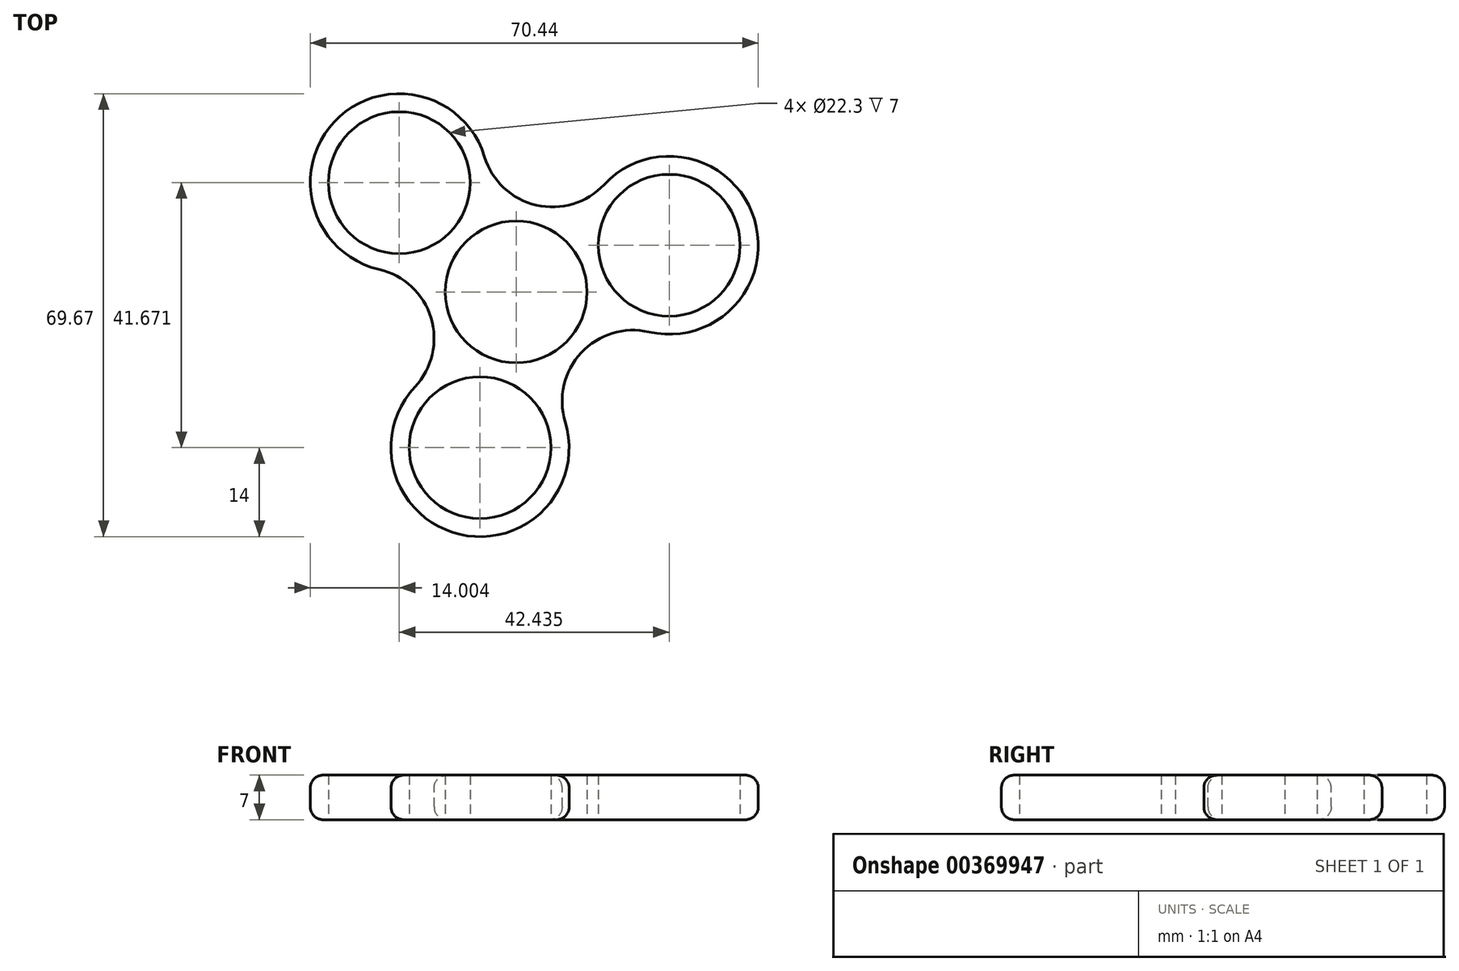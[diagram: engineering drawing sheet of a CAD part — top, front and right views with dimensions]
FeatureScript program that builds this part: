
annotation { "Feature Type Name" : "Feature", "Feature Type Description" : "" }
export const myFeature = defineFeature(function(context is Context, id is Id, definition is map)
    precondition{}
    {
        {
            var Q0;
            Q0=qCreatedBy(makeId("Top.planeOp"),FACE);
            var sketch = newSketch(context, id + "F0", { "sketchPlane" : qUnion([Q0])});
            skCircle(sketch, "E0", {"center": v(0, 0) * mm, "radius": 11.15 * mm});
            skLineSegment(sketch, "E1", {"start": v(0, 0) * mm, "end": v(-18.38, 17.17) * mm});
            skLineSegment(sketch, "E2", {"start": v(0, 0) * mm, "end": v(24.06, 7.33) * mm});
            skLineSegment(sketch, "E3", {"start": v(0, 0) * mm, "end": v(-5.68, -24.5) * mm});
            skCircle(sketch, "E4", {"center": v(-18.38, 17.17) * mm, "radius": 11.15 * mm});
            skCircle(sketch, "E5", {"center": v(24.06, 7.33) * mm, "radius": 11.15 * mm});
            skCircle(sketch, "E6", {"center": v(-5.68, -24.5) * mm, "radius": 11.15 * mm});
            skCircle(sketch, "E7", {"center": v(0, 0) * mm, "radius": 14 * mm});
            skCircle(sketch, "E8", {"center": v(-18.38, 17.17) * mm, "radius": 14 * mm});
            skCircle(sketch, "E9", {"center": v(24.06, 7.33) * mm, "radius": 14 * mm});
            skCircle(sketch, "E10", {"center": v(-5.68, -24.5) * mm, "radius": 14 * mm});
            skLineSegment(sketch, "E11", {"start": v(-18.38, 17.17) * mm, "end": v(-8.82, 27.4) * mm});
            skLineSegment(sketch, "E12", {"start": v(24.06, 7.33) * mm, "end": v(19.98, 20.72) * mm});
            skLineSegment(sketch, "E13", {"start": v(-5.68, -24.5) * mm, "end": v(7.96, -27.66) * mm});
            skLineSegment(sketch, "E14", {"start": v(-5.68, -24.5) * mm, "end": v(-19.32, -21.34) * mm});
            skLineSegment(sketch, "E15", {"start": v(-18.38, 17.17) * mm, "end": v(-27.93, 6.94) * mm});
            skLineSegment(sketch, "E16", {"start": v(24.06, 7.33) * mm, "end": v(28.14, -6.06) * mm});
            skArc(sketch, "E17", {"start": v(-8.82, 27.4) * mm, "mid": v(3.16, 13.64) * mm, "end": v(19.98, 20.72) * mm});
            skArc(sketch, "E18", {"start": v(-19.32, -21.34) * mm, "mid": v(-13.4, -4.08) * mm, "end": v(-27.93, 6.94) * mm});
            skArc(sketch, "E19", {"start": v(28.14, -6.06) * mm, "mid": v(10.23, -9.56) * mm, "end": v(7.96, -27.66) * mm});
            skSolve(sketch);
        }
        {
            var Q0;
            {var subQ0=sQuery(id+"F0.wireOp",EDGE,"E15");var subQ1=sQuery(id+"F0.wireOp",EDGE,"E4");var subQ2=makeQuery(id+"F0.imprint","INTERSECT",VERTEX,{"derivedFrom":[subQ1,subQ0]});Q0=makeQuery(id+"F0.imprint","IMPRINT",FACE,{"disambiguationData":[TD([[makeQuery(id+"F0.imprint","IMPRINT",EDGE,{"disambiguationData":[TD([[subQ2,1.0]])],"derivedFrom":subQ1}),-1.0]])]});}
            var Q1;
            {var subQ0=sQuery(id+"F0.wireOp",EDGE,"E17");var subQ2=sQuery(id+"F0.wireOp",EDGE,"E8");var subQ6=makeQuery(id+"F0.imprint","INTERSECT",VERTEX,{"derivedFrom":[subQ2,subQ0]});Q1=makeQuery(id+"F0.imprint","IMPRINT",FACE,{"disambiguationData":[TD([[makeQuery(id+"F0.imprint","IMPRINT",EDGE,{"disambiguationData":[TD([[subQ6,1.0]])],"derivedFrom":subQ2}),1.0]])]});}
            var Q2;
            {var subQ0=sQuery(id+"F0.wireOp",EDGE,"E8");var subQ3=sQuery(id+"F0.wireOp",EDGE,"E7");var subQ5=makeQuery(id+"F0.imprint","INTERSECT",VERTEX,{"disambiguationData":[OD(0.0)],"derivedFrom":[subQ3,subQ0]});Q2=makeQuery(id+"F0.imprint","IMPRINT",FACE,{"disambiguationData":[TD([[makeQuery(id+"F0.imprint","IMPRINT",EDGE,{"disambiguationData":[TD([[subQ5,-1.0]])],"derivedFrom":subQ3}),1.0]])]});}
            var Q3;
            {var subQ0=sQuery(id+"F0.wireOp",EDGE,"E8");var subQ3=sQuery(id+"F0.wireOp",EDGE,"E7");var subQ5=makeQuery(id+"F0.imprint","INTERSECT",VERTEX,{"disambiguationData":[OD(1.0)],"derivedFrom":[subQ3,subQ0]});Q3=makeQuery(id+"F0.imprint","IMPRINT",FACE,{"disambiguationData":[TD([[makeQuery(id+"F0.imprint","IMPRINT",EDGE,{"disambiguationData":[TD([[subQ5,1.0]])],"derivedFrom":subQ3}),1.0]])]});}
            var Q4;
            {var subQ0=sQuery(id+"F0.wireOp",EDGE,"E18");var subQ1=sQuery(id+"F0.wireOp",EDGE,"E8");var subQ2=makeQuery(id+"F0.imprint","INTERSECT",VERTEX,{"derivedFrom":[subQ1,subQ0]});Q4=makeQuery(id+"F0.imprint","IMPRINT",FACE,{"disambiguationData":[TD([[makeQuery(id+"F0.imprint","IMPRINT",EDGE,{"disambiguationData":[TD([[subQ2,-1.0]])],"derivedFrom":subQ1}),1.0]])]});}
            var Q5;
            {var subQ0=sQuery(id+"F0.wireOp",EDGE,"E18");var subQ2=sQuery(id+"F0.wireOp",EDGE,"E10");var subQ6=makeQuery(id+"F0.imprint","INTERSECT",VERTEX,{"derivedFrom":[subQ2,subQ0]});Q5=makeQuery(id+"F0.imprint","IMPRINT",FACE,{"disambiguationData":[TD([[makeQuery(id+"F0.imprint","IMPRINT",EDGE,{"disambiguationData":[TD([[subQ6,1.0]])],"derivedFrom":subQ2}),1.0]])]});}
            var Q6;
            {var subQ0=sQuery(id+"F0.wireOp",EDGE,"E10");var subQ3=sQuery(id+"F0.wireOp",EDGE,"E7");var subQ5=makeQuery(id+"F0.imprint","INTERSECT",VERTEX,{"disambiguationData":[OD(0.0)],"derivedFrom":[subQ3,subQ0]});Q6=makeQuery(id+"F0.imprint","IMPRINT",FACE,{"disambiguationData":[TD([[makeQuery(id+"F0.imprint","IMPRINT",EDGE,{"disambiguationData":[TD([[subQ5,-1.0]])],"derivedFrom":subQ3}),1.0]])]});}
            var Q7;
            {var subQ0=sQuery(id+"F0.wireOp",EDGE,"E10");var subQ3=sQuery(id+"F0.wireOp",EDGE,"E7");var subQ5=makeQuery(id+"F0.imprint","INTERSECT",VERTEX,{"disambiguationData":[OD(1.0)],"derivedFrom":[subQ3,subQ0]});Q7=makeQuery(id+"F0.imprint","IMPRINT",FACE,{"disambiguationData":[TD([[makeQuery(id+"F0.imprint","IMPRINT",EDGE,{"disambiguationData":[TD([[subQ5,1.0]])],"derivedFrom":subQ3}),1.0]])]});}
            var Q8;
            {var subQ0=sQuery(id+"F0.wireOp",EDGE,"E19");var subQ1=sQuery(id+"F0.wireOp",EDGE,"E10");var subQ2=makeQuery(id+"F0.imprint","INTERSECT",VERTEX,{"derivedFrom":[subQ1,subQ0]});Q8=makeQuery(id+"F0.imprint","IMPRINT",FACE,{"disambiguationData":[TD([[makeQuery(id+"F0.imprint","IMPRINT",EDGE,{"disambiguationData":[TD([[subQ2,-1.0]])],"derivedFrom":subQ1}),1.0]])]});}
            var Q9;
            {var subQ0=sQuery(id+"F0.wireOp",EDGE,"E14");var subQ1=sQuery(id+"F0.wireOp",EDGE,"E6");var subQ2=makeQuery(id+"F0.imprint","INTERSECT",VERTEX,{"derivedFrom":[subQ1,subQ0]});Q9=makeQuery(id+"F0.imprint","IMPRINT",FACE,{"disambiguationData":[TD([[makeQuery(id+"F0.imprint","IMPRINT",EDGE,{"disambiguationData":[TD([[subQ2,-1.0]])],"derivedFrom":subQ1}),-1.0]])]});}
            var Q10;
            {var subQ1=sQuery(id+"F0.wireOp",EDGE,"E7");var subQ5=makeQuery(id+"F0.imprint","INTERSECT",VERTEX,{"derivedFrom":[subQ1,sQuery(id+"F0.wireOp",EDGE,"E18")]});Q10=makeQuery(id+"F0.imprint","IMPRINT",FACE,{"disambiguationData":[TD([[makeQuery(id+"F0.imprint","IMPRINT",EDGE,{"disambiguationData":[TD([[subQ5,1.0]])],"derivedFrom":subQ1}),1.0]])]});}
            var Q11;
            {var subQ1=sQuery(id+"F0.wireOp",EDGE,"E7");var subQ5=makeQuery(id+"F0.imprint","INTERSECT",VERTEX,{"derivedFrom":[subQ1,sQuery(id+"F0.wireOp",EDGE,"E19")]});Q11=makeQuery(id+"F0.imprint","IMPRINT",FACE,{"disambiguationData":[TD([[makeQuery(id+"F0.imprint","IMPRINT",EDGE,{"disambiguationData":[TD([[subQ5,1.0]])],"derivedFrom":subQ1}),1.0]])]});}
            var Q12;
            {var subQ0=sQuery(id+"F0.wireOp",EDGE,"E9");var subQ3=sQuery(id+"F0.wireOp",EDGE,"E7");var subQ5=makeQuery(id+"F0.imprint","INTERSECT",VERTEX,{"disambiguationData":[OD(1.0)],"derivedFrom":[subQ3,subQ0]});Q12=makeQuery(id+"F0.imprint","IMPRINT",FACE,{"disambiguationData":[TD([[makeQuery(id+"F0.imprint","IMPRINT",EDGE,{"disambiguationData":[TD([[subQ5,-1.0]])],"derivedFrom":subQ3}),1.0]])]});}
            var Q13;
            {var subQ0=sQuery(id+"F0.wireOp",EDGE,"E9");var subQ3=sQuery(id+"F0.wireOp",EDGE,"E7");var subQ5=makeQuery(id+"F0.imprint","INTERSECT",VERTEX,{"disambiguationData":[OD(0.0)],"derivedFrom":[subQ3,subQ0]});Q13=makeQuery(id+"F0.imprint","IMPRINT",FACE,{"disambiguationData":[TD([[makeQuery(id+"F0.imprint","IMPRINT",EDGE,{"disambiguationData":[TD([[subQ5,1.0]])],"derivedFrom":subQ3}),1.0]])]});}
            var Q14;
            {var subQ1=sQuery(id+"F0.wireOp",EDGE,"E7");var subQ5=makeQuery(id+"F0.imprint","INTERSECT",VERTEX,{"derivedFrom":[subQ1,sQuery(id+"F0.wireOp",EDGE,"E17")]});Q14=makeQuery(id+"F0.imprint","IMPRINT",FACE,{"disambiguationData":[TD([[makeQuery(id+"F0.imprint","IMPRINT",EDGE,{"disambiguationData":[TD([[subQ5,1.0]])],"derivedFrom":subQ1}),1.0]])]});}
            var Q15;
            {var subQ0=sQuery(id+"F0.wireOp",EDGE,"E17");var subQ2=sQuery(id+"F0.wireOp",EDGE,"E9");var subQ6=makeQuery(id+"F0.imprint","INTERSECT",VERTEX,{"derivedFrom":[subQ2,subQ0]});Q15=makeQuery(id+"F0.imprint","IMPRINT",FACE,{"disambiguationData":[TD([[makeQuery(id+"F0.imprint","IMPRINT",EDGE,{"disambiguationData":[TD([[subQ6,-1.0]])],"derivedFrom":subQ2}),1.0]])]});}
            var Q16;
            {var subQ0=sQuery(id+"F0.wireOp",EDGE,"E12");var subQ1=sQuery(id+"F0.wireOp",EDGE,"E5");var subQ2=makeQuery(id+"F0.imprint","INTERSECT",VERTEX,{"derivedFrom":[subQ1,subQ0]});Q16=makeQuery(id+"F0.imprint","IMPRINT",FACE,{"disambiguationData":[TD([[makeQuery(id+"F0.imprint","IMPRINT",EDGE,{"disambiguationData":[TD([[subQ2,1.0]])],"derivedFrom":subQ1}),-1.0]])]});}
            var Q17;
            {var subQ0=sQuery(id+"F0.wireOp",EDGE,"E19");var subQ2=sQuery(id+"F0.wireOp",EDGE,"E9");var subQ9=makeQuery(id+"F0.imprint","INTERSECT",VERTEX,{"derivedFrom":[subQ2,subQ0]});Q17=makeQuery(id+"F0.imprint","IMPRINT",FACE,{"disambiguationData":[TD([[makeQuery(id+"F0.imprint","IMPRINT",EDGE,{"disambiguationData":[TD([[subQ9,1.0]])],"derivedFrom":subQ2}),1.0]])]});}
            var Q18;
            {var subQ0=sQuery(id+"F0.wireOp",EDGE,"E17");var subQ1=sQuery(id+"F0.wireOp",EDGE,"E9");var subQ3=makeQuery(id+"F0.imprint","INTERSECT",VERTEX,{"derivedFrom":[subQ1,subQ0]});Q18=makeQuery(id+"F0.imprint","IMPRINT",FACE,{"disambiguationData":[TD([[makeQuery(id+"F0.imprint","IMPRINT",EDGE,{"disambiguationData":[TD([[subQ3,1.0]])],"derivedFrom":subQ1}),1.0]])]});}
            var Q19;
            {var subQ0=sQuery(id+"F0.wireOp",EDGE,"E17");var subQ1=sQuery(id+"F0.wireOp",EDGE,"E8");var subQ3=makeQuery(id+"F0.imprint","INTERSECT",VERTEX,{"derivedFrom":[subQ1,subQ0]});Q19=makeQuery(id+"F0.imprint","IMPRINT",FACE,{"disambiguationData":[TD([[makeQuery(id+"F0.imprint","IMPRINT",EDGE,{"disambiguationData":[TD([[subQ3,-1.0]])],"derivedFrom":subQ1}),1.0]])]});}
            var Q20;
            {var subQ0=sQuery(id+"F0.wireOp",EDGE,"E18");var subQ1=sQuery(id+"F0.wireOp",EDGE,"E8");var subQ3=makeQuery(id+"F0.imprint","INTERSECT",VERTEX,{"derivedFrom":[subQ1,subQ0]});Q20=makeQuery(id+"F0.imprint","IMPRINT",FACE,{"disambiguationData":[TD([[makeQuery(id+"F0.imprint","IMPRINT",EDGE,{"disambiguationData":[TD([[subQ3,1.0]])],"derivedFrom":subQ1}),1.0]])]});}
            var Q21;
            {var subQ0=sQuery(id+"F0.wireOp",EDGE,"E18");var subQ1=sQuery(id+"F0.wireOp",EDGE,"E10");var subQ3=makeQuery(id+"F0.imprint","INTERSECT",VERTEX,{"derivedFrom":[subQ1,subQ0]});Q21=makeQuery(id+"F0.imprint","IMPRINT",FACE,{"disambiguationData":[TD([[makeQuery(id+"F0.imprint","IMPRINT",EDGE,{"disambiguationData":[TD([[subQ3,-1.0]])],"derivedFrom":subQ1}),1.0]])]});}
            var Q22;
            {var subQ0=sQuery(id+"F0.wireOp",EDGE,"E19");var subQ1=sQuery(id+"F0.wireOp",EDGE,"E9");var subQ3=makeQuery(id+"F0.imprint","INTERSECT",VERTEX,{"derivedFrom":[subQ1,subQ0]});Q22=makeQuery(id+"F0.imprint","IMPRINT",FACE,{"disambiguationData":[TD([[makeQuery(id+"F0.imprint","IMPRINT",EDGE,{"disambiguationData":[TD([[subQ3,-1.0]])],"derivedFrom":subQ1}),1.0]])]});}
            var Q23;
            {var subQ0=sQuery(id+"F0.wireOp",EDGE,"E19");var subQ1=sQuery(id+"F0.wireOp",EDGE,"E10");var subQ3=makeQuery(id+"F0.imprint","INTERSECT",VERTEX,{"derivedFrom":[subQ1,subQ0]});Q23=makeQuery(id+"F0.imprint","IMPRINT",FACE,{"disambiguationData":[TD([[makeQuery(id+"F0.imprint","IMPRINT",EDGE,{"disambiguationData":[TD([[subQ3,1.0]])],"derivedFrom":subQ1}),1.0]])]});}
            extrude(context, id + "F1", {"entities" : qUnion([Q0, Q1, Q2, Q3, Q4, Q5, Q6, Q7, Q8, Q9, Q10, Q11, Q12, Q13, Q14, Q15, Q16, Q17, Q18, Q19, Q20, Q21, Q22, Q23]), "depth" : 7 * mm, "offsetDistance" : 25 * mm});
        }
        {
            var Q0;
            {var subQ0=sQuery(id+"F0.wireOp",EDGE,"E8");var subQ1=sQuery(id+"F0.wireOp",EDGE,"E7");Q0=makeQuery(id+"F1.opExtrude","SWEPT_EDGE",EDGE,{"disambiguationData":[OSD([subQ1,subQ0]),TDD([makeQuery(id+"F0.imprint","INTERSECT",VERTEX,{"disambiguationData":[OD(1.0)],"derivedFrom":[subQ1,subQ0]})])]});}
            var Q1;
            {var subQ0=sQuery(id+"F0.wireOp",EDGE,"E10");var subQ1=sQuery(id+"F0.wireOp",EDGE,"E7");Q1=makeQuery(id+"F1.opExtrude","SWEPT_EDGE",EDGE,{"disambiguationData":[OSD([subQ1,subQ0]),TDD([makeQuery(id+"F0.imprint","INTERSECT",VERTEX,{"disambiguationData":[OD(0.0)],"derivedFrom":[subQ1,subQ0]})])]});}
            var Q2;
            {var subQ0=sQuery(id+"F0.wireOp",EDGE,"E9");var subQ1=sQuery(id+"F0.wireOp",EDGE,"E7");Q2=makeQuery(id+"F1.opExtrude","SWEPT_EDGE",EDGE,{"disambiguationData":[OSD([subQ1,subQ0]),TDD([makeQuery(id+"F0.imprint","INTERSECT",VERTEX,{"disambiguationData":[OD(0.0)],"derivedFrom":[subQ1,subQ0]})])]});}
            var Q3;
            {var subQ0=sQuery(id+"F0.wireOp",EDGE,"E8");var subQ1=sQuery(id+"F0.wireOp",EDGE,"E7");Q3=makeQuery(id+"F1.opExtrude","SWEPT_EDGE",EDGE,{"disambiguationData":[OSD([subQ1,subQ0]),TDD([makeQuery(id+"F0.imprint","INTERSECT",VERTEX,{"disambiguationData":[OD(0.0)],"derivedFrom":[subQ1,subQ0]})])]});}
            var Q4;
            {var subQ0=sQuery(id+"F0.wireOp",EDGE,"E9");var subQ1=sQuery(id+"F0.wireOp",EDGE,"E7");Q4=makeQuery(id+"F1.opExtrude","SWEPT_EDGE",EDGE,{"disambiguationData":[OSD([subQ1,subQ0]),TDD([makeQuery(id+"F0.imprint","INTERSECT",VERTEX,{"disambiguationData":[OD(1.0)],"derivedFrom":[subQ1,subQ0]})])]});}
            var Q5;
            {var subQ0=sQuery(id+"F0.wireOp",EDGE,"E10");var subQ1=sQuery(id+"F0.wireOp",EDGE,"E7");Q5=makeQuery(id+"F1.opExtrude","SWEPT_EDGE",EDGE,{"disambiguationData":[OSD([subQ1,subQ0]),TDD([makeQuery(id+"F0.imprint","INTERSECT",VERTEX,{"disambiguationData":[OD(1.0)],"derivedFrom":[subQ1,subQ0]})])]});}
            fillet(context, id + "F2", {"entities" : qUnion([Q0, Q1, Q2, Q3, Q4, Q5]), "radius" : 11.15 * mm, "tangentPropagation" : true, "allowEdgeOverflow" : false});
        }
        {
            var Q0;
            Q0=makeQuery(id+"F1.opExtrude","CAP_EDGE",EDGE,{"disambiguationData":[OSD([sQuery(id+"F0.wireOp",EDGE,"E10")])],"isStart":false});
            var Q1;
            Q1=makeQuery(id+"F1.opExtrude","CAP_EDGE",EDGE,{"disambiguationData":[OSD([sQuery(id+"F0.wireOp",EDGE,"E10")])],"isStart":true});
            fillet(context, id + "F3", {"entities" : qUnion([Q0, Q1]), "radius" : 2 * mm, "tangentPropagation" : true, "allowEdgeOverflow" : false});
        }
    });
